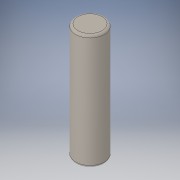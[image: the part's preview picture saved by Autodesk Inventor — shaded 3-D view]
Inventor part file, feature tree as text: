
AUTODESK INVENTOR PART (.ipt)
format: ipt  version: 2018 (Build 220112000, 112)  size: 115,712 bytes
history: native  units: in
note: dims shown in document units (in); Inventor stores cm internally (conversion verified against a paired STEP export)
features: revolve x1
ambient origin geometry x8: Origin, YZ Plane, XZ Plane, XY Plane, X Axis, Y Axis, Z Axis, Center Point
bodies: Solid1 (feature_tree)
feature tree (1):
  revolve  "Revolve1"  [1 undecoded]
note: 1 required parameter value undecoded (feature->parameter linkage not recoverable at this tier; creation-order binding heuristic only, values carry confidence <= 0.55)
